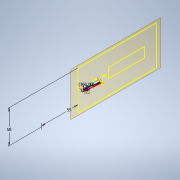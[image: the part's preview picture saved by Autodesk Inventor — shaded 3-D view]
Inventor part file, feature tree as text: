
AUTODESK INVENTOR PART (.ipt)
format: ipt  version: 2021 (Build 250183000, 183)  size: 412,160 bytes
history: native  units: mm
features: sketch x12, other x12, sweep x4, reference x2
ambient origin geometry x8: Origin, YZ Plane, XZ Plane, XY Plane, X Axis, Y Axis, Z Axis, Center Point
bodies: Body1 (feature_tree)
feature tree (30):
  sketch  "Szkic1"
  other  "Płaszczyzna konstrukcyjna1"
  sketch  "Szkic2"
  other  "Płaszczyzna konstrukcyjna2"
  sketch  "Szkic3"
  sketch  "Szkic 3D1"
  other  "Płaszczyzna konstrukcyjna3"
  sketch  "Szkic4"
  other  "Płaszczyzna konstrukcyjna4"
  sketch  "Szkic5"
  other  "Płaszczyzna konstrukcyjna5"
  sweep  "Przeciągnięcie2"
  sweep  "Przeciągnięcie3"
  sweep  "Przeciągnięcie4"
  other  "Płaszczyzna konstrukcyjna6"
  sweep  "Przeciągnięcie5"
  sketch  "Szkic 3D3"
  other  "Płaszczyzna konstrukcyjna7"
  sketch  "Szkic8"
  other  "Płaszczyzna konstrukcyjna8"
  sketch  "Szkic9"
  reference  "Odniesienie1"
  sketch  "Szkic6"
  sketch  "Szkic7"
  sketch  "Szkic 3D2"
  reference  "Odniesienie2"
  parser-record x1  (decoder bookkeeping rows leaked as tree rows — omitted from the tree; the rows remain in map.json)
  other  "model tensometru.iam"
  other  "zalany_tensometr:1"
  other  "podstwa:1"
note: 1 file-system path scrubbed to <path> (originals preserved in map.json)
